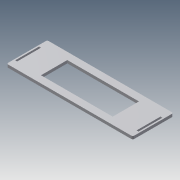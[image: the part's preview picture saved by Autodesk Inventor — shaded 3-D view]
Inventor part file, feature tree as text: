
AUTODESK INVENTOR PART (.ipt)
format: ipt  version: 2014 (Build 180170000, 170)  size: 110,080 bytes
history: native  units: mm
features: extrude x3, sketch x3, fillet x1
ambient origin geometry x8: Origin, YZ Plane, XZ Plane, XY Plane, X Axis, Y Axis, Z Axis, Center Point
bodies: Solid1 (feature_tree)
feature tree (7):
  extrude  "Extrusion1"  Depth=264.0mm
  extrude  "Extrusion2"  Depth=258.0mm
  fillet  "Fillet1"  Radius=3.0mm
  extrude  "Extrusion5"  Depth=50.0mm
  sketch  "Sketch1"  dims[d0=85.0mm d1=264.0mm]
  sketch  "Sketch2"  dims[d2=6.0mm d3=0.0mm d4=258.0mm d5=3.0mm]
  sketch  "Sketch4"  dims[d6=4.0mm d7=50.0mm d8=15.0mm d9=4.0mm d10=0.0mm d11=3.0mm d30=10.0mm d31=0.0mm d32=50.0mm d33=15.0mm]
